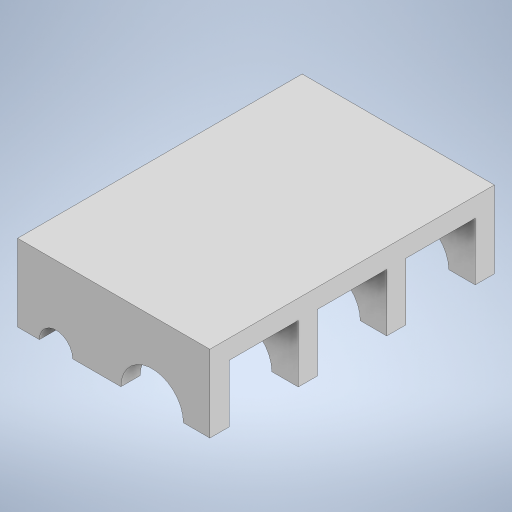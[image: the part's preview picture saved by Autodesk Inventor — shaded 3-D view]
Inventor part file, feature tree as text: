
AUTODESK INVENTOR PART (.ipt)
format: ipt  version: 2023 (Build 270158000, 158)  size: 260,608 bytes
history: native  units: in
note: dims shown in document units (in); Inventor stores cm internally (conversion verified against a paired STEP export)
features: extrude x2, sketch x1
ambient origin geometry x8: Origin, YZ Plane, XZ Plane, XY Plane, X Axis, Y Axis, Z Axis, Center Point
bodies: Solid1 (feature_tree)
feature tree (3):
  extrude  "Extrusion1"  Depth=0.5in
  extrude  "Extrusion2"  Depth=7.4in TaperAngle=0.0deg
  sketch  "Sketch1"  dims[d0=5.0in d2=1.625in d3=7.4in d4=0.0in d15=1.4in d16=3.7in d17=6.0in d18=0.5in d20=2.528in d21=7.4in d22=0.0in d25=1.5in d26=0.866in d31=1.2546in d32=0.5669in d33=2.0in d34=1.5in d27=0.5in d28=0.0344in d29=0.0in d30=0.0in]
